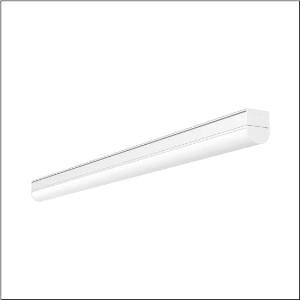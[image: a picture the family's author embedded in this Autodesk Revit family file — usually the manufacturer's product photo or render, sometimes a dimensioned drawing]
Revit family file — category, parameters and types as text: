
# Revit family: ecopack_r__31_51lj12dnm80a_c0ee
name_source: partatom
category: Lighting Fixtures
units: mm (PartAtom-declared; Revit-internal decimal feet)

## family parameters
Cut with Voids When Loaded = No
Host = Face
Light Source = No
Part Type = Normal
Room Calculation Point = No
Round Connector Dimension = Use Diameter
Shared = No

## types (1)
- --- (1 x LED, 6780 lm, 52 W, 5000K)
    Apparent Load = 52 VA
    CIE Flux Codes = 39 67 87 89 100
    Color Rendering = 80
    Color Temperature = 5000K
    Default Elevation = 1800 mm
    Description = Ecopack® 31, diffuser luminaire, primary optical cover: cover, of PC, frosted, light emission: direct distribution, primary light characteristic: symmetric, installation type: surface-mounted, LED, rated luminous flux: 7.000lm, luminous efficacy: 135lm/W, light colour: 830/840/850, colour temperature: 3000/4000/5000K, control gear: ECG DALI, with terminal, 5-pole, mains connection: 220..240V, AC, 50/60Hz, rated input power: 52W, housing, of aluminium, traffic white (RAL 9016), length: 1.450mm, width: 56mm, height: 68mm, end cap, of PC, white, protection rating (complete): IP20, insulation class (complete): insulation class I (protective earthing), certification: CE, impact resistance: IK06, permissible operating ambient temperature: -20..+40°C, packaging unit: 1 piece
    Height = 68 mm
    Lamp = 1 x LED
    Lamp Light Flux = 6780 lm
    Lamp Power = 52 W
    Lamp count = 1
    Length = 1450 mm
    Luminous efficacy = 130 lm/W
    Manufacturer = Siteco
    ModVariant = No
    Model = 51LJ12DNM80A
    Mounting Place = Ceiling
    Mounting Type = Surface mounted
    Number of Poles = 1
    OnlyDefault = Yes
    Power Factor = 1
    Product Name = Ecopack® 31
    Product group = diffuser luminaire
    ProductGroupID = 304
    Protection Class = Protection class I
    Protection Degree = IP 20
    RLX_Detail_Level = 1
    RLX_Emergency_Light_Flux = 0 lm
    RLX_Emergency_Type = 0
    RLX_Emergency_Type_DB = No
    RlxData = <blob elided: 21613 chars, md5=92893464>
    Socket = socket
    Standby Power = 0 W
    System Light Flux = 6780 lm
    System Power = 52 W
    Type Comments = individual setting: colour temperature 5000K
    Type Image = l_1007033.jpg
    URL = http://relux.com
    VarID = @adj_124871
    Voltage = 0 V
    Weight = 0.00 kg
    Width = 56 mm

## geometry (parser evidence)
native form markers: Blend x4, Sweep x13
no freeform markers — native parametric forms only
